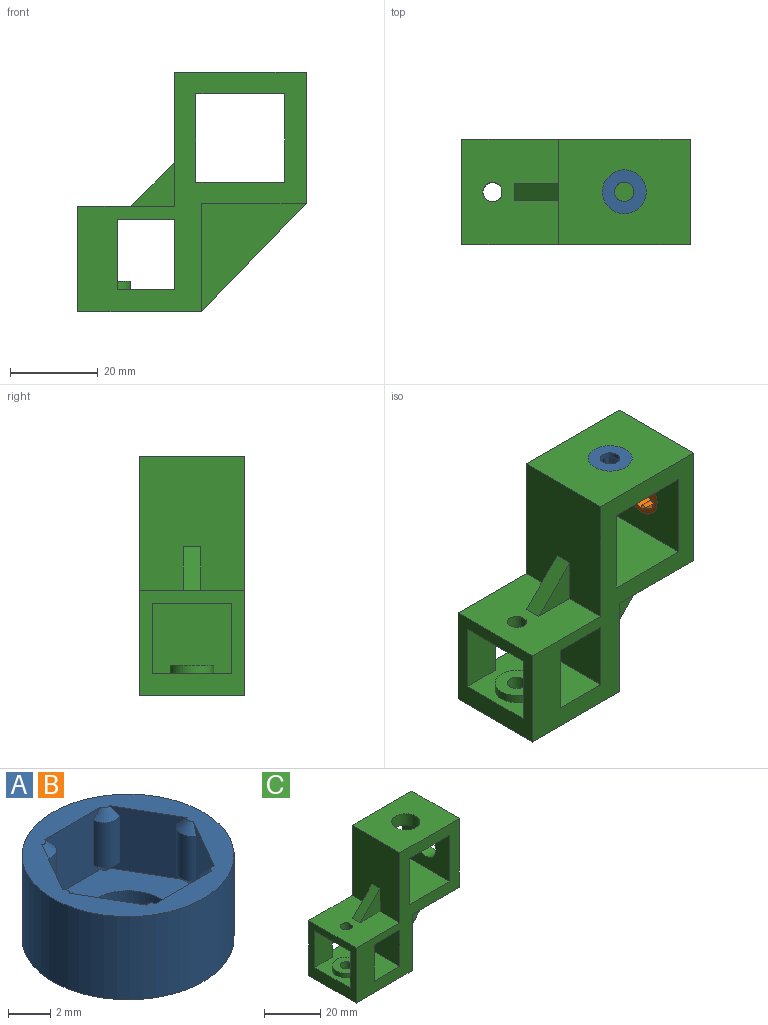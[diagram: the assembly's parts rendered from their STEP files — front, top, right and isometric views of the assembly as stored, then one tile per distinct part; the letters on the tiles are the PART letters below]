
ASSEMBLY  parts=3 mates=2
PART A: 29 faces, bbox 10x10x4.8 mm
  f0: plane 3.77x3.6mm, normal (0,-1,0), area 10.5mm2, adj f7,f8,f9,f10,f17,f18,f19,f26
  f1: plane 3.6x3.27mm, normal (-0.87,-0.5,0), area 10.5mm2, adj f7,f8,f9,f10,f14,f15,f16,f26
  f2: plane 3.6x3.27mm, normal (-0.87,0.5,0), area 10.5mm2, adj f7,f11,f12,f13,f14,f15,f16,f26
  f3: plane 3.77x3.6mm, normal (0,1,0), area 10.5mm2, adj f7,f11,f12,f13,f23,f24,f25,f26
  f4: plane 3.6x3.27mm, normal (0.87,0.5,0), area 10.5mm2, adj f7,f20,f21,f22,f23,f24,f25,f26
  f5: cylinder r=5mm len=10mm, axis (0,0,-1), area 150.8mm2, adj f7,f27
  f6: plane 3.6x3.27mm, normal (0.87,-0.5,0), area 10.5mm2, adj f7,f17,f18,f19,f20,f21,f22,f26
  f7: plane 10x10mm, normal (0,0,1), area 31.5mm2, adj f0,f1,f2,f3,f4,f5,f6,f9
  f8: cylinder r=0.75mm len=2.6mm, axis (0,0,-1), area 4.1mm2, adj f0,f1,f9,f10
  f9: cone r=0.25mm half-angle=45deg, axis (0,0,-1), area 0.7mm2, adj f0,f1,f7,f8
  f10: cone r=0.75mm half-angle=45deg, axis (0,0,1), area 0.7mm2, adj f0,f1,f8,f26
  f11: cylinder r=0.75mm len=2.6mm, axis (0,0,-1), area 4.1mm2, adj f2,f3,f12,f13
  f12: cone r=0.25mm half-angle=45deg, axis (0,0,-1), area 0.7mm2, adj f2,f3,f7,f11
  f13: cone r=0.75mm half-angle=45deg, axis (0,0,1), area 0.7mm2, adj f2,f3,f11,f26
  f14: cylinder r=0.75mm len=2.6mm, axis (0,0,-1), area 4.1mm2, adj f1,f2,f15,f16
  f15: cone r=0.25mm half-angle=45deg, axis (0,0,-1), area 0.7mm2, adj f1,f2,f7,f14
  f16: cone r=0.75mm half-angle=45deg, axis (0,0,1), area 0.7mm2, adj f1,f2,f14,f26
  f17: cone r=0.75mm half-angle=45deg, axis (0,0,1), area 0.7mm2, adj f0,f6,f19,f26
  f18: cone r=0.25mm half-angle=45deg, axis (0,0,-1), area 0.7mm2, adj f0,f6,f7,f19
  f19: cylinder r=0.75mm len=2.6mm, axis (0,0,-1), area 4.1mm2, adj f0,f6,f17,f18
  f20: cone r=0.75mm half-angle=45deg, axis (0,0,1), area 0.7mm2, adj f4,f6,f22,f26
  f21: cone r=0.25mm half-angle=45deg, axis (0,0,-1), area 0.7mm2, adj f4,f6,f7,f22
  f22: cylinder r=0.75mm len=2.6mm, axis (0,0,-1), area 4.1mm2, adj f4,f6,f20,f21
  f23: cylinder r=0.75mm len=2.6mm, axis (0,0,-1), area 4.1mm2, adj f3,f4,f24,f25
  f24: cone r=0.25mm half-angle=45deg, axis (0,0,-1), area 0.7mm2, adj f3,f4,f7,f23
  f25: cone r=0.75mm half-angle=45deg, axis (0,0,1), area 0.7mm2, adj f3,f4,f23,f26
  f26: plane 8.29x7.4mm, normal (0,0,1), area 31.8mm2, adj f0,f1,f2,f3,f4,f6,f10,f13
  f27: plane 10x10mm, normal (0,0,-1), area 63.3mm2, adj f5,f28
  f28: cylinder r=2.2mm len=4.4mm, axis (0,0,-1), area 16.6mm2, adj f26,f27
PART B: same geometry as A
PART C: 36 faces, bbox 52x24x54.6 mm
  f0: plane 30.6x24mm, normal (-1,0,0), area 694.4mm2, adj f4,f5,f6,f20,f21,f22,f33
  f1: plane 24x16mm, normal (-1,0,0), area 384mm2, adj f4,f5,f23,f30
  f2: plane 23.84x10mm, normal (0,0,-1), area 238.4mm2, adj f5,f8,f16,f18
  f3: plane 24.6x10mm, normal (1,0,0), area 246mm2, adj f4,f7,f15,f19
  f4: plane 54.6x52mm, normal (0,1,0), area 963.4mm2, adj f0,f1,f3,f6,f7,f8,f9,f10
  f5: plane 54.6x52mm, normal (0,-1,0), area 963.4mm2, adj f0,f1,f2,f6,f8,f9,f10,f11
  f6: plane 30x24mm, normal (0,0,1), area 641.5mm2, adj f0,f4,f5,f8,f13
  f7: plane 23.84x10mm, normal (0,0,-1), area 238.4mm2, adj f3,f4,f8,f19
  f8: plane 30x24mm, normal (1,0,0), area 641.5mm2, adj f2,f4,f5,f6,f7,f14,f17
  f9: plane 24x20.2mm, normal (0,0,-1), area 406.3mm2, adj f4,f5,f10,f12,f13
  f10: plane 24x20.2mm, normal (-1,0,0), area 406.3mm2, adj f4,f5,f9,f11,f14
  f11: plane 24x20.2mm, normal (0,0,1), area 484.8mm2, adj f4,f5,f10,f12
  f12: plane 24x20.2mm, normal (1,0,0), area 484.8mm2, adj f4,f5,f9,f11
  f13: cylinder r=5mm len=10mm, axis (0,0,1), area 153.9mm2, adj f6,f9
  f14: cylinder r=5mm len=10mm, axis (1,0,0), area 153.9mm2, adj f8,f10
  f15: plane 28.16x24mm, normal (0,0,-1), area 660.6mm2, adj f3,f4,f5,f16,f17,f26,f27
  f16: plane 24.6x10mm, normal (1,0,0), area 246mm2, adj f2,f5,f15,f18
  f17: plane 24.6x23.84mm, normal (0.72,0,-0.7), area 137mm2, adj f8,f15,f18,f19
  f18: plane 24.6x23.84mm, normal (0,-1,0), area 293.3mm2, adj f2,f16,f17
  f19: plane 24.6x23.84mm, normal (0,1,0), area 293.3mm2, adj f3,f7,f17
  f20: plane 10x10mm, normal (-0.71,0,0.71), area 56.6mm2, adj f0,f21,f22,f33
  f21: plane 10x10mm, normal (0,-1,0), area 50mm2, adj f0,f20,f33
  f22: plane 10x10mm, normal (0,1,0), area 50mm2, adj f0,f20,f33
  f23: plane 24x22mm, normal (0,0,1), area 395.5mm2, adj f1,f4,f5,f24,f26,f28,f29,f31
  f24: cylinder r=5mm len=10mm, axis (0,0,1), area 62.8mm2, adj f23,f25
  f25: plane 10x10mm, normal (0,0,1), area 63.3mm2, adj f24,f27
  f26: plane 24x24mm, normal (-1,0,0), area 288mm2, adj f4,f5,f15,f23,f28,f30,f31,f33
  f27: cylinder r=2.2mm len=7mm, axis (0,0,1), area 96.8mm2, adj f15,f25
  f28: plane 16x9mm, normal (0,-1,0), area 144mm2, adj f23,f26,f29,f30
  f29: plane 16x3mm, normal (1,0,0), area 48mm2, adj f4,f23,f28,f30
  f30: plane 24x22mm, normal (0,0,-1), area 459mm2, adj f1,f4,f5,f26,f28,f29,f31,f32
  f31: plane 16x9mm, normal (0,1,0), area 144mm2, adj f23,f26,f30,f32
  f32: plane 16x3mm, normal (1,0,0), area 48mm2, adj f5,f23,f30,f31
  f33: plane 24x22mm, normal (0,0,1), area 473mm2, adj f0,f4,f5,f20,f21,f22,f26,f34
  f34: cylinder r=2.2mm len=4.4mm, axis (0,0,1), area 35.8mm2, adj f30,f33,f35
  f35: plane 3x1.83mm, normal (-1,0,0), area 5.5mm2, adj f30,f33,f34
PLACE A rot(axis=(1,0,0),180deg) t=(15,0,13.8)mm
PLACE B rot(axis=(0,-1,0),90deg) t=(28.8,0,0)mm
PLACE C at identity
MATE fastened A.f5 <-> C.f13  axis (0,0,1) through (15,0,15)mm
MATE fastened B.f5 <-> C.f14  axis (1,0,0) through (30,0,0)mm
